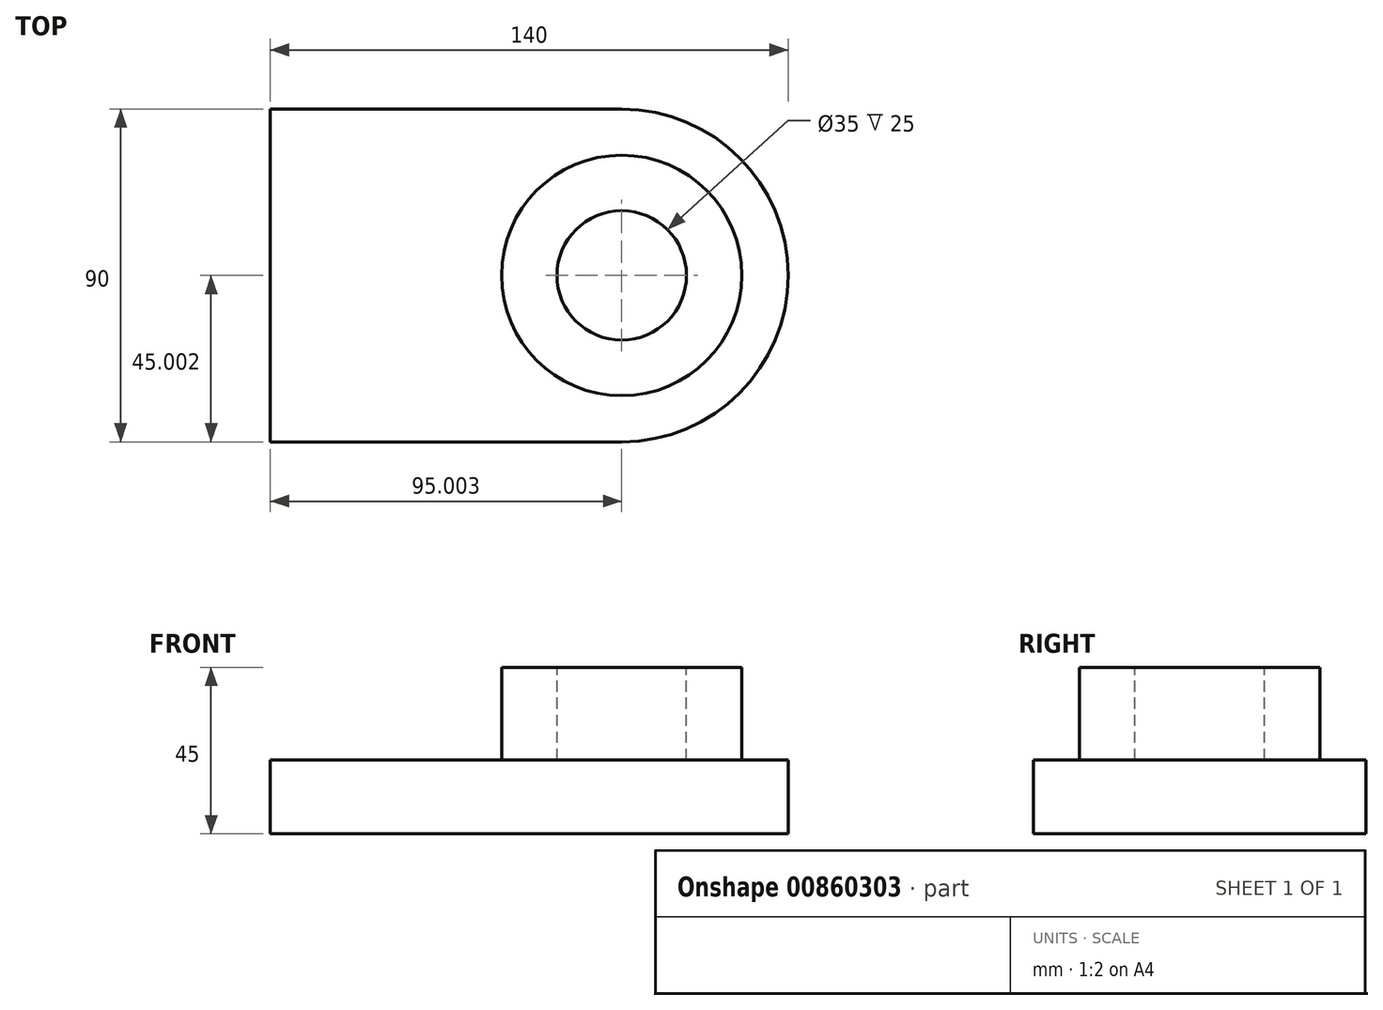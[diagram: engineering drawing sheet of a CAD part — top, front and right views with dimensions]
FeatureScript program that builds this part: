
annotation { "Feature Type Name" : "Feature", "Feature Type Description" : "" }
export const myFeature = defineFeature(function(context is Context, id is Id, definition is map)
    precondition{}
    {
        {
            var Q0;
            Q0=qCreatedBy(makeId("Top.planeOp"),FACE);
            var sketch = newSketch(context, id + "F0", { "sketchPlane" : qUnion([Q0])});
            skLineSegment(sketch, "E0.bottom", {"start": v(-48.55, 52.06) * mm, "end": v(46.45, 52.06) * mm});
            skLineSegment(sketch, "E0.top", {"start": v(-48.55, -37.94) * mm, "end": v(46.45, -37.94) * mm});
            skLineSegment(sketch, "E0.left", {"start": v(-48.55, 52.06) * mm, "end": v(-48.55, -37.94) * mm});
            skLineSegment(sketch, "E0.right", {"start": v(46.45, 52.06) * mm, "end": v(46.45, -37.94) * mm});
            skArc(sketch, "E1", {"start": v(46.45, 52.06) * mm, "mid": v(91.45, 7.06) * mm, "end": v(46.45, -37.94) * mm});
            skSolve(sketch);
        }
        {
            var Q0;
            Q0 = qSketchRegion(id + "F0", true);
            extrude(context, id + "F1", {"entities" : qUnion([Q0]), "depth" : 20 * mm, "offsetDistance" : 25.4 * mm});
        }
        {
            var Q0;
            Q0=makeQuery(id+"F1.opExtrude","CAP_FACE",FACE,{"disambiguationData":[OSD([sQuery(id+"F0.wireOp",EDGE,"E0.bottom"),sQuery(id+"F0.wireOp",EDGE,"E0.top"),sQuery(id+"F0.wireOp",EDGE,"E0.left"),sQuery(id+"F0.wireOp",EDGE,"E1")])],"isStart":false});
            var sketch = newSketch(context, id + "F2", { "sketchPlane" : qUnion([Q0])});
            skCircle(sketch, "E2", {"center": v(46.45, 7.06) * mm, "radius": 32.5 * mm});
            skSolve(sketch);
        }
        {
            var Q0;
            Q0 = qSketchRegion(id + "F2", true);
            extrude(context, id + "F3", {"entities" : qUnion([Q0]), "operationType" : NewBodyOperationType.ADD, "depth" : 25 * mm, "offsetDistance" : 25.4 * mm});
        }
        {
            var Q0;
            Q0=makeQuery(id+"F3.opExtrude","CAP_FACE",FACE,{"disambiguationData":[OSD([sQuery(id+"F2.wireOp",EDGE,"E2")])],"isStart":false});
            var sketch = newSketch(context, id + "F4", { "sketchPlane" : qUnion([Q0])});
            skCircle(sketch, "E3", {"center": v(46.45, 7.06) * mm, "radius": 17.5 * mm});
            skSolve(sketch);
        }
        {
            var Q0;
            Q0 = qSketchRegion(id + "F4", true);
            extrude(context, id + "F5", {"entities" : qUnion([Q0]), "operationType" : NewBodyOperationType.REMOVE, "oppositeDirection" : true, "depth" : 25 * mm, "offsetDistance" : 25.4 * mm});
        }
    });
